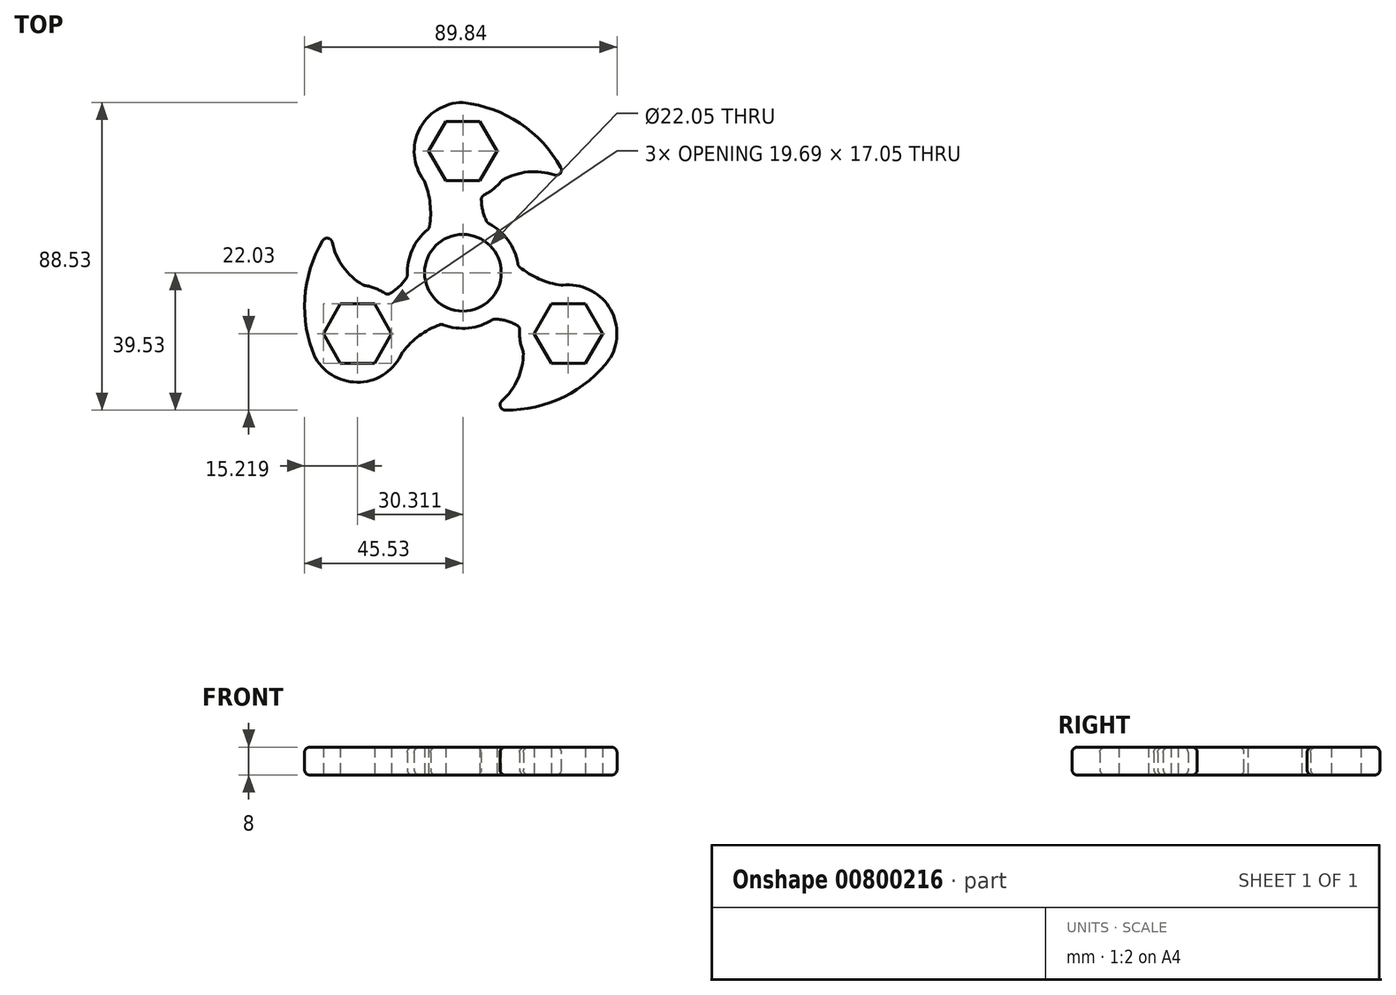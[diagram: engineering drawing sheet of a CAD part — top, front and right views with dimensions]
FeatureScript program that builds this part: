
annotation { "Feature Type Name" : "Feature", "Feature Type Description" : "" }
export const myFeature = defineFeature(function(context is Context, id is Id, definition is map)
    precondition{}
    {
        {
            var Q0;
            Q0=qCreatedBy(makeId("Top.planeOp"),FACE);
            var sketch = newSketch(context, id + "F0", { "sketchPlane" : qUnion([Q0])});
            skCircle(sketch, "E0", {"center": v(0, 0) * mm, "radius": 11.03 * mm});
            skLineSegment(sketch, "E1", {"start": v(0, 0) * mm, "end": v(0, 35) * mm, "construction": true});
            skCircle(sketch, "E2.cCircle", {"center": v(0, 35) * mm, "radius": 8.53 * mm, "construction": true});
            skLineSegment(sketch, "E2.0", {"start": v(-4.92, 43.53) * mm, "end": v(4.92, 43.53) * mm});
            skLineSegment(sketch, "E2.1", {"start": v(4.92, 43.53) * mm, "end": v(9.84, 35) * mm});
            skLineSegment(sketch, "E2.2", {"start": v(9.84, 35) * mm, "end": v(4.92, 26.48) * mm});
            skLineSegment(sketch, "E2.3", {"start": v(4.92, 26.48) * mm, "end": v(-4.92, 26.48) * mm});
            skLineSegment(sketch, "E2.4", {"start": v(-4.92, 26.48) * mm, "end": v(-9.84, 35) * mm});
            skLineSegment(sketch, "E2.5", {"start": v(-9.84, 35) * mm, "end": v(-4.92, 43.53) * mm});
            skPoint(sketch, "E2.0.midPoint", {"position": v(0, 43.53) * mm});
            skCircle(sketch, "E3", {"center": v(0, 0) * mm, "radius": 16 * mm});
            skArc(sketch, "E4", {"start": v(-9.72, 12.7) * mm, "mid": v(-9.4, 19.7) * mm, "end": v(-11.12, 26.5) * mm});
            skArc(sketch, "E5", {"start": v(5.31, 22.05) * mm, "mid": v(5.66, 18.1) * mm, "end": v(7.04, 14.37) * mm});
            skCircle(sketch, "E6", {"center": v(0, 35) * mm, "radius": 14 * mm});
            skLineSegment(sketch, "E7", {"start": v(0, 26.48) * mm, "end": v(30, 26.48) * mm, "construction": true});
            skArc(sketch, "E8", {"start": v(30, 26.48) * mm, "mid": v(18.07, 41.83) * mm, "end": v(0, 49) * mm});
            skArc(sketch, "E9", {"start": v(30, 26.48) * mm, "mid": v(20.55, 29.09) * mm, "end": v(11.1, 26.48) * mm});
            skSolve(sketch);
        }
        {
            var Q0;
            Q0=makeQuery(id+"F0.imprint","IMPRINT",FACE,{"disambiguationData":[TD([[makeQuery(id+"F0.imprint","IMPRINT",EDGE,{"derivedFrom":sQuery(id+"F0.wireOp",EDGE,"E2.0")}),1.0]])]});
            var Q1;
            {var subQ0=sQuery(id+"F0.wireOp",EDGE,"E8");Q1=makeQuery(id+"F0.imprint","IMPRINT",FACE,{"disambiguationData":[TD([[makeQuery(id+"F0.imprint","IMPRINT",EDGE,{"derivedFrom":subQ0}),1.0]])]});}
            var Q2;
            {var subQ0=sQuery(id+"F0.wireOp",EDGE,"E4");Q2=makeQuery(id+"F0.imprint","IMPRINT",FACE,{"disambiguationData":[TD([[makeQuery(id+"F0.imprint","IMPRINT",EDGE,{"derivedFrom":subQ0}),-1.0]])]});}
            var Q3;
            Q3=makeQuery(id+"F0.imprint","IMPRINT",FACE,{"disambiguationData":[TD([[makeQuery(id+"F0.imprint","IMPRINT",EDGE,{"derivedFrom":sQuery(id+"F0.wireOp",EDGE,"E0")}),-1.0]])]});
            extrude(context, id + "F1", {"entities" : qUnion([Q0, Q1, Q2, Q3]), "endBound" : BoundingType.SYMMETRIC, "depth" : 8 * mm, "offsetDistance" : 25 * mm});
        }
        {
            var Q0;
            Q0=makeQuery(id+"F3.opPattern","COPY",FACE,{"derivedFrom":makeQuery(id+"F1.opExtrude","SWEPT_FACE",FACE,{"disambiguationData":[OSD([sQuery(id+"F0.wireOp",EDGE,"E8")])]}),"instanceName":"1"});
            var Q1;
            {var subQ0=sQuery(id+"F0.wireOp",EDGE,"E6");Q1=makeQuery(id+"F3.opPattern","COPY",FACE,{"derivedFrom":makeQuery(id+"F1.opExtrude","SWEPT_FACE",FACE,{"disambiguationData":[OSD([subQ0]),TDD([makeQuery(id+"F0.imprint","IMPRINT",EDGE,{"disambiguationData":[TD([[makeQuery(id+"F0.imprint","INTERSECT",VERTEX,{"derivedFrom":[sQuery(id+"F0.wireOp",EDGE,"E4"),subQ0]}),1.0]])],"derivedFrom":subQ0})])]}),"instanceName":"1"});}
            var Q2;
            Q2=makeQuery(id+"F3.opPattern","COPY",FACE,{"derivedFrom":makeQuery(id+"F1.opExtrude","SWEPT_FACE",FACE,{"disambiguationData":[OSD([sQuery(id+"F0.wireOp",EDGE,"E9")])]}),"instanceName":"2"});
            var Q3;
            {var subQ4=sQuery(id+"F0.wireOp",EDGE,"E4");var subQ5=sQuery(id+"F0.wireOp",EDGE,"E3");Q3=makeQuery(id+"F3.boolean.opBoolean","SPLIT",FACE,{"disambiguationData":[TD([makeQuery(id+"F3.opPattern","COPY",FACE,{"derivedFrom":makeQuery(id+"F1.opExtrude","SWEPT_FACE",FACE,{"disambiguationData":[OSD([subQ4])]}),"instanceName":"1"})])],"derivedFrom":makeQuery(id+"F1.opExtrude","SWEPT_FACE",FACE,{"disambiguationData":[OSD([subQ5])]})});}
            var Q4;
            {var subQ0=sQuery(id+"F0.wireOp",EDGE,"E4");var subQ5=sQuery(id+"F0.wireOp",EDGE,"E3");Q4=makeQuery(id+"F3.boolean.opBoolean","SPLIT",FACE,{"disambiguationData":[TD([makeQuery(id+"F1.opExtrude","SWEPT_FACE",FACE,{"disambiguationData":[OSD([subQ0])]})])],"derivedFrom":makeQuery(id+"F1.opExtrude","SWEPT_FACE",FACE,{"disambiguationData":[OSD([subQ5])]})});}
            var Q5;
            {var subQ0=sQuery(id+"F0.wireOp",EDGE,"E6");Q5=makeQuery(id+"F1.opExtrude","SWEPT_FACE",FACE,{"disambiguationData":[OSD([subQ0]),TDD([makeQuery(id+"F0.imprint","IMPRINT",EDGE,{"disambiguationData":[TD([[makeQuery(id+"F0.imprint","INTERSECT",VERTEX,{"derivedFrom":[sQuery(id+"F0.wireOp",EDGE,"E4"),subQ0]}),1.0]])],"derivedFrom":subQ0})])]});}
            var Q6;
            Q6=makeQuery(id+"F1.opExtrude","SWEPT_FACE",FACE,{"disambiguationData":[OSD([sQuery(id+"F0.wireOp",EDGE,"E9")])]});
            var Q7;
            {var subQ3=sQuery(id+"F0.wireOp",EDGE,"E5");var subQ5=sQuery(id+"F0.wireOp",EDGE,"E3");Q7=makeQuery(id+"F3.boolean.opBoolean","SPLIT",FACE,{"disambiguationData":[TD([makeQuery(id+"F1.opExtrude","SWEPT_FACE",FACE,{"disambiguationData":[OSD([subQ3])]})])],"derivedFrom":makeQuery(id+"F1.opExtrude","SWEPT_FACE",FACE,{"disambiguationData":[OSD([subQ5])]})});}
            var Q8;
            {var subQ0=sQuery(id+"F0.wireOp",EDGE,"E6");Q8=makeQuery(id+"F3.opPattern","COPY",FACE,{"derivedFrom":makeQuery(id+"F1.opExtrude","SWEPT_FACE",FACE,{"disambiguationData":[OSD([subQ0]),TDD([makeQuery(id+"F0.imprint","IMPRINT",EDGE,{"disambiguationData":[TD([[makeQuery(id+"F0.imprint","INTERSECT",VERTEX,{"derivedFrom":[sQuery(id+"F0.wireOp",EDGE,"E4"),subQ0]}),1.0]])],"derivedFrom":subQ0})])]}),"instanceName":"2"});}
            var Q9;
            Q9=makeQuery(id+"F3.opPattern","COPY",FACE,{"derivedFrom":makeQuery(id+"F1.opExtrude","SWEPT_FACE",FACE,{"disambiguationData":[OSD([sQuery(id+"F0.wireOp",EDGE,"E9")])]}),"instanceName":"1"});
            var Q10;
            Q10=makeQuery(id+"F1.opExtrude","SWEPT_FACE",FACE,{"disambiguationData":[OSD([sQuery(id+"F0.wireOp",EDGE,"E4")])]});
            var Q11;
            {var subQ0=sQuery(id+"F0.wireOp",EDGE,"E6");Q11=makeQuery(id+"F1.opExtrude","SWEPT_FACE",FACE,{"disambiguationData":[OSD([subQ0]),TDD([makeQuery(id+"F0.imprint","IMPRINT",EDGE,{"disambiguationData":[TD([[makeQuery(id+"F0.imprint","INTERSECT",VERTEX,{"derivedFrom":[sQuery(id+"F0.wireOp",EDGE,"E5"),subQ0]}),-1.0]])],"derivedFrom":subQ0})])]});}
            var Q12;
            Q12=makeQuery(id+"F1.opExtrude","SWEPT_FACE",FACE,{"disambiguationData":[OSD([sQuery(id+"F0.wireOp",EDGE,"E5")])]});
            var Q13;
            Q13=makeQuery(id+"F1.opExtrude","SWEPT_FACE",FACE,{"disambiguationData":[OSD([sQuery(id+"F0.wireOp",EDGE,"E8")])]});
            fillet(context, id + "F2", {"entities" : qUnion([Q0, Q1, Q2, Q3, Q4, Q5, Q6, Q7, Q8, Q9, Q10, Q11, Q12, Q13]), "radius" : 1.5 * mm, "tangentPropagation" : true, "allowEdgeOverflow" : false});
        }
        {
            var Q0;
            Q0=makeQuery(id+"F1.opExtrude","SWEPT_BODY",BODY,{"disambiguationData":[OSD([sQuery(id+"F0.wireOp",EDGE,"E0"),sQuery(id+"F0.wireOp",EDGE,"E2.0"),sQuery(id+"F0.wireOp",EDGE,"E2.1"),sQuery(id+"F0.wireOp",EDGE,"E2.2"),sQuery(id+"F0.wireOp",EDGE,"E2.3"),sQuery(id+"F0.wireOp",EDGE,"E2.4"),sQuery(id+"F0.wireOp",EDGE,"E2.5"),sQuery(id+"F0.wireOp",EDGE,"E3"),sQuery(id+"F0.wireOp",EDGE,"E4"),sQuery(id+"F0.wireOp",EDGE,"E5"),sQuery(id+"F0.wireOp",EDGE,"E6"),sQuery(id+"F0.wireOp",EDGE,"E8"),sQuery(id+"F0.wireOp",EDGE,"E9")])]});
            var Q1;
            Q1=makeQuery(id+"F1.opExtrude","CAP_EDGE",EDGE,{"disambiguationData":[OSD([sQuery(id+"F0.wireOp",EDGE,"E0")])],"isStart":false});
            circularPattern(context, id + "F3", {"operationType" : NewBodyOperationType.ADD, "entities" : qUnion([Q0]), "axis" : qUnion([Q1]), "angle" : 360 * degree, "instanceCount" : 3, "equalSpace" : true});
        }
    });
